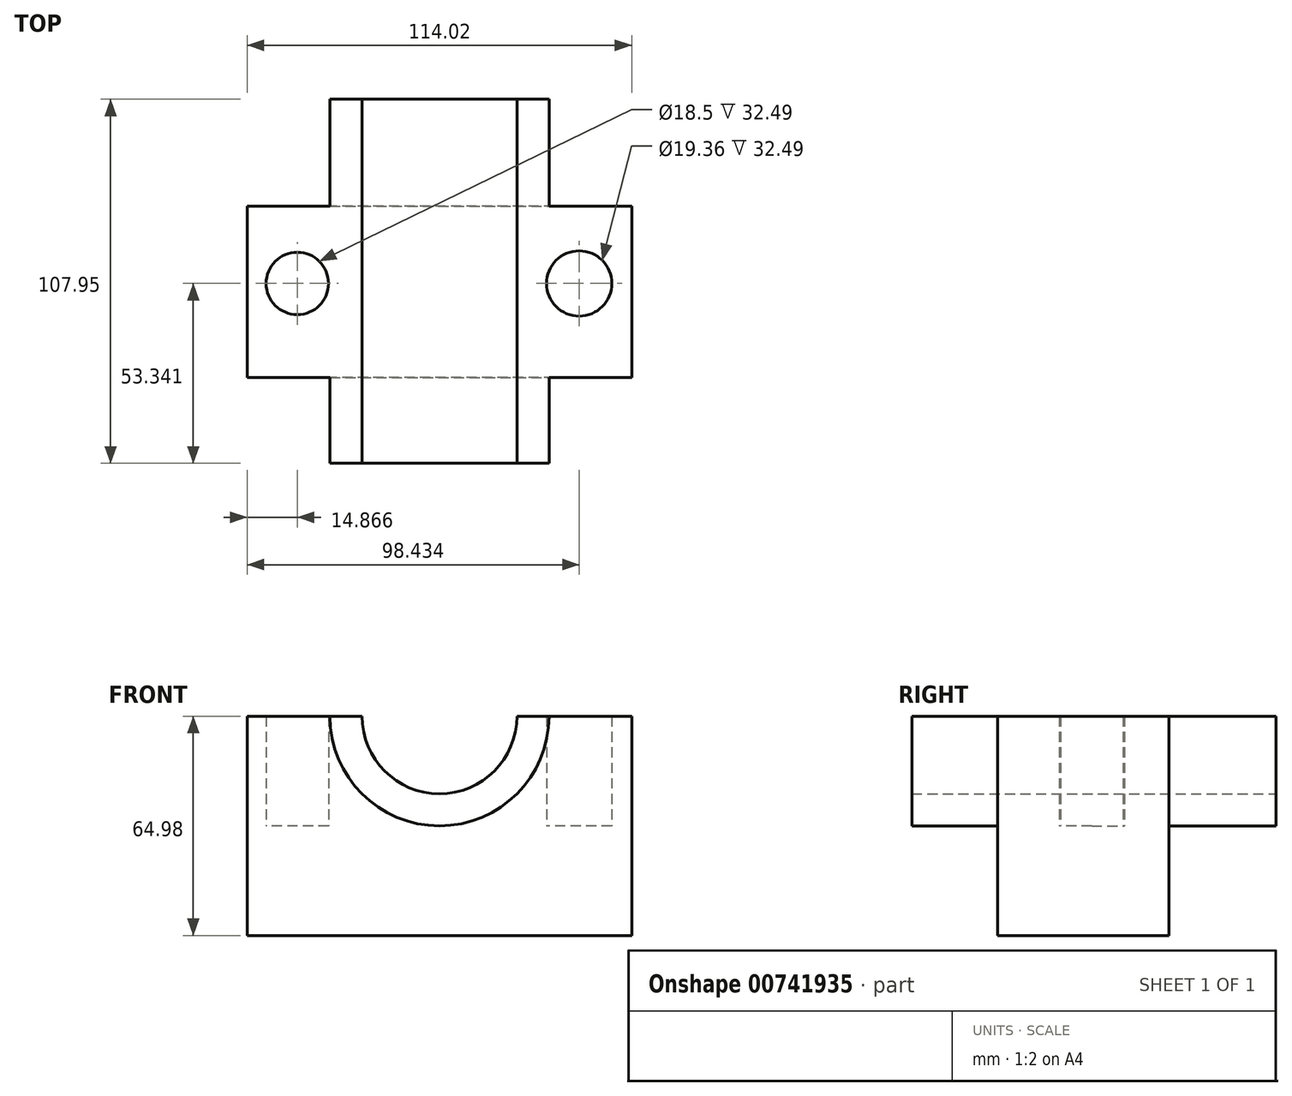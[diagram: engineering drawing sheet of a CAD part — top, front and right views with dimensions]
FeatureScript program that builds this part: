
annotation { "Feature Type Name" : "Feature", "Feature Type Description" : "" }
export const myFeature = defineFeature(function(context is Context, id is Id, definition is map)
    precondition{}
    {
        {
            var Q0;
            Q0=qCreatedBy(makeId("Front.planeOp"),FACE);
            var sketch = newSketch(context, id + "F0", { "sketchPlane" : qUnion([Q0])});
            skLineSegment(sketch, "E0.bottom", {"start": v(57, 32.49) * mm, "end": v(-57, 32.49) * mm});
            skLineSegment(sketch, "E0.top", {"start": v(57, -32.49) * mm, "end": v(-57, -32.49) * mm});
            skLineSegment(sketch, "E0.left", {"start": v(57, 32.49) * mm, "end": v(57, -32.49) * mm});
            skLineSegment(sketch, "E0.right", {"start": v(-57, 32.49) * mm, "end": v(-57, -32.49) * mm});
            skPoint(sketch, "E0.middle", {"position": v(0, 0) * mm});
            skArc(sketch, "E1", {"start": v(-32.49, 32.49) * mm, "mid": v(0, 0) * mm, "end": v(32.49, 32.49) * mm});
            skArc(sketch, "E2", {"start": v(-22.96, 32.49) * mm, "mid": v(0, 9.53) * mm, "end": v(22.96, 32.49) * mm});
            skSolve(sketch);
        }
        {
            var Q0;
            Q0=makeQuery(id+"F0.imprint","IMPRINT",FACE,{"disambiguationData":[TD([[makeQuery(id+"F0.imprint","IMPRINT",EDGE,{"derivedFrom":sQuery(id+"F0.wireOp",EDGE,"E0.top")}),-1.0]])]});
            extrude(context, id + "F1", {"entities" : qUnion([Q0]), "depth" : 50.8 * mm, "offsetDistance" : 25.4 * mm});
        }
        {
            var Q0;
            {var subQ0=sQuery(id+"F0.wireOp",EDGE,"E1");Q0=makeQuery(id+"F0.imprint","IMPRINT",FACE,{"disambiguationData":[TD([[makeQuery(id+"F0.imprint","IMPRINT",EDGE,{"derivedFrom":subQ0}),1.0]])]});}
            extrude(context, id + "F2", {"entities" : qUnion([Q0]), "operationType" : NewBodyOperationType.ADD, "depth" : 76.2 * mm, "offsetDistance" : 25.4 * mm});
        }
        {
            var Q0;
            {var subQ0=sQuery(id+"F0.wireOp",EDGE,"E2");Q0=makeQuery(id+"F0.imprint","IMPRINT",FACE,{"disambiguationData":[TD([[makeQuery(id+"F0.imprint","IMPRINT",EDGE,{"derivedFrom":subQ0}),1.0]])]});}
            extrude(context, id + "F3", {"entities" : qUnion([Q0]), "operationType" : NewBodyOperationType.REMOVE, "oppositeDirection" : true, "depth" : 25.4 * mm, "offsetDistance" : 25.4 * mm});
        }
        {
            var Q0;
            {var subQ0=sQuery(id+"F0.wireOp",EDGE,"E1");Q0=makeQuery(id+"F0.imprint","IMPRINT",FACE,{"disambiguationData":[TD([[makeQuery(id+"F0.imprint","IMPRINT",EDGE,{"derivedFrom":subQ0}),1.0]])]});}
            extrude(context, id + "F4", {"entities" : qUnion([Q0]), "operationType" : NewBodyOperationType.ADD, "oppositeDirection" : true, "depth" : 31.75 * mm, "offsetDistance" : 25.4 * mm});
        }
        {
            var Q0;
            {var subQ0=sQuery(id+"F0.wireOp",EDGE,"E2");Q0=makeQuery(id+"F0.imprint","IMPRINT",FACE,{"disambiguationData":[TD([[makeQuery(id+"F0.imprint","IMPRINT",EDGE,{"derivedFrom":subQ0}),1.0]])]});}
            extrude(context, id + "F5", {"entities" : qUnion([Q0]), "operationType" : NewBodyOperationType.REMOVE, "oppositeDirection" : true, "depth" : 25.4 * mm, "offsetDistance" : 25.4 * mm});
        }
        {
            var Q0;
            Q0=qCreatedBy(makeId("Top.planeOp"),FACE);
            var sketch = newSketch(context, id + "F6", { "sketchPlane" : qUnion([Q0])});
            skCircle(sketch, "E3", {"center": v(-42.14, -22.86) * mm, "radius": 9.25 * mm});
            skCircle(sketch, "E4", {"center": v(41.42, -22.86) * mm, "radius": 9.68 * mm});
            skSolve(sketch);
        }
        {
            var Q0;
            Q0 = qSketchRegion(id + "F6", true);
            extrude(context, id + "F7", {"entities" : qUnion([Q0]), "operationType" : NewBodyOperationType.REMOVE, "depth" : 50.8 * mm, "offsetDistance" : 25.4 * mm});
        }
    });
